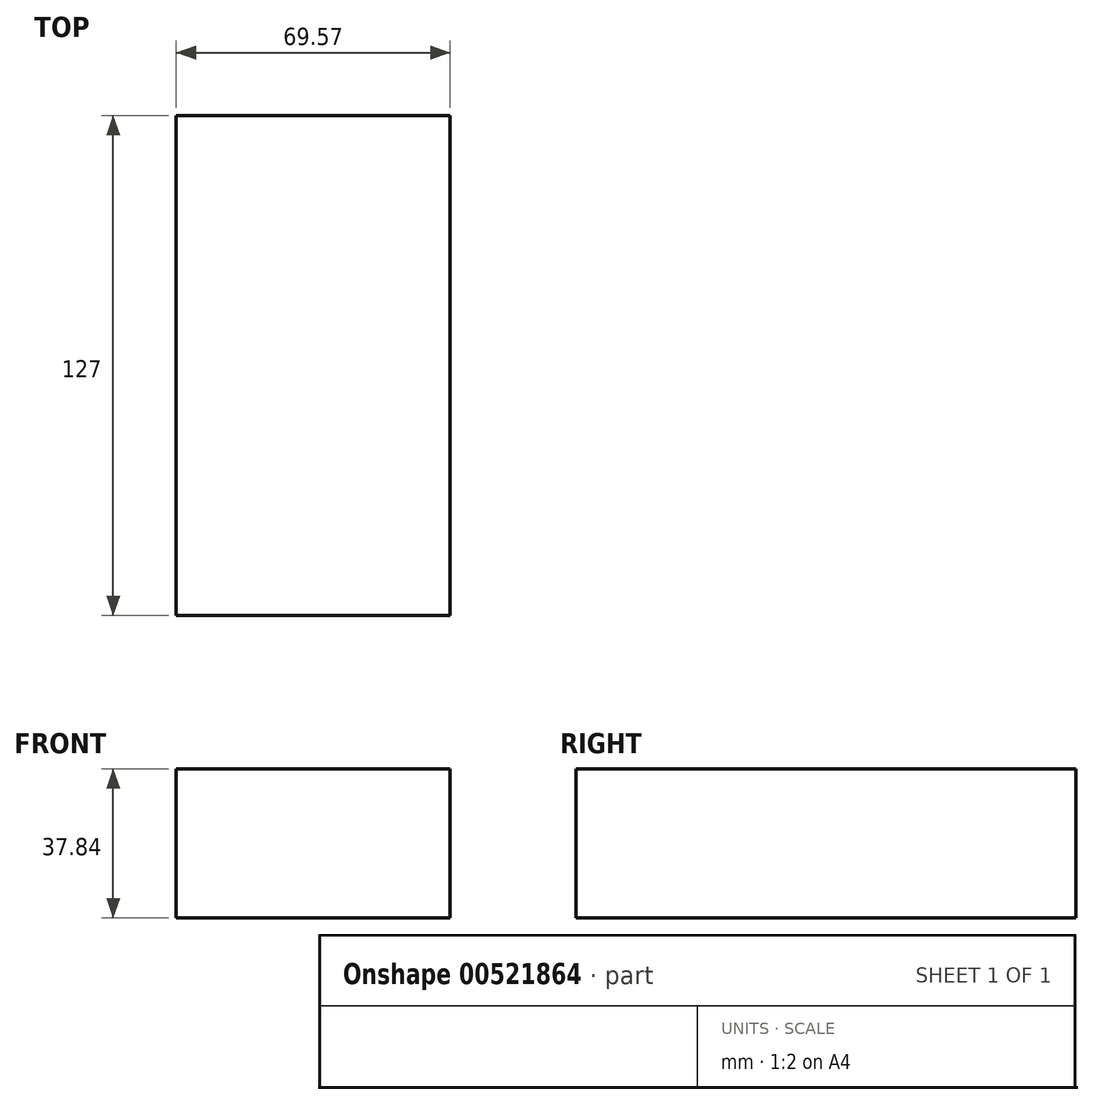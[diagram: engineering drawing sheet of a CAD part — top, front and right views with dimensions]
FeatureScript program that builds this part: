
annotation { "Feature Type Name" : "Feature", "Feature Type Description" : "" }
export const myFeature = defineFeature(function(context is Context, id is Id, definition is map)
    precondition{}
    {
        {
            var Q0;
            Q0=qCreatedBy(makeId("Front.planeOp"),FACE);
            var sketch = newSketch(context, id + "F0", { "sketchPlane" : qUnion([Q0])});
            skLineSegment(sketch, "E0.bottom", {"start": v(-22.27, 15.37) * mm, "end": v(47.3, 15.37) * mm});
            skLineSegment(sketch, "E0.top", {"start": v(-22.27, -22.47) * mm, "end": v(47.3, -22.47) * mm});
            skLineSegment(sketch, "E0.left", {"start": v(-22.27, 15.37) * mm, "end": v(-22.27, -22.47) * mm});
            skLineSegment(sketch, "E0.right", {"start": v(47.3, 15.37) * mm, "end": v(47.3, -22.47) * mm});
            skSolve(sketch);
        }
        {
            var Q0;
            Q0=makeQuery(id+"F0.imprint","IMPRINT",FACE,{"disambiguationData":[TD([[makeQuery(id+"F0.imprint","IMPRINT",EDGE,{"derivedFrom":sQuery(id+"F0.wireOp",EDGE,"E0.bottom")}),-1.0]])]});
            extrude(context, id + "F1", {"entities" : qUnion([Q0]), "depth" : 127 * mm, "offsetDistance" : 25.4 * mm});
        }
    });
